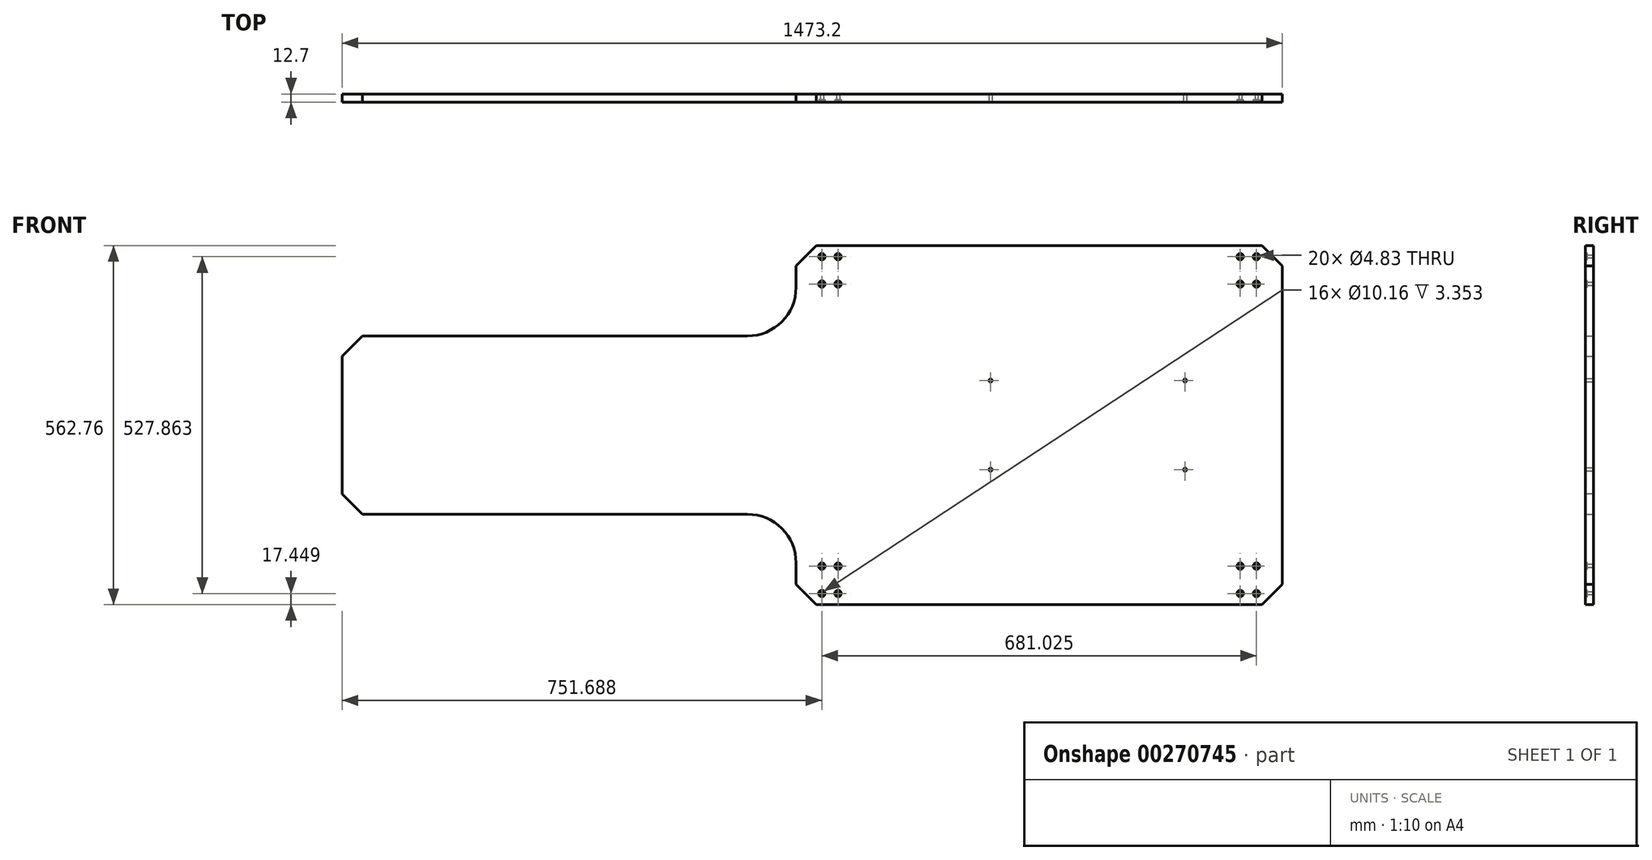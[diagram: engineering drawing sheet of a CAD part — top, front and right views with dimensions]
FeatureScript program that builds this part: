
annotation { "Feature Type Name" : "Feature", "Feature Type Description" : "" }
export const myFeature = defineFeature(function(context is Context, id is Id, definition is map)
    precondition{}
    {
        {
            var Q0;
            Q0=qCreatedBy(makeId("Front.planeOp"),FACE);
            var sketch = newSketch(context, id + "F0", { "sketchPlane" : qUnion([Q0])});
            skLineSegment(sketch, "E0.bottom", {"start": v(381, 281.38) * mm, "end": v(-381, 281.38) * mm});
            skLineSegment(sketch, "E0.top", {"start": v(381, -281.38) * mm, "end": v(-381, -281.38) * mm});
            skLineSegment(sketch, "E0.left", {"start": v(381, 281.38) * mm, "end": v(381, -281.38) * mm});
            skLineSegment(sketch, "E0.right", {"start": v(-381, 281.38) * mm, "end": v(-381, 139.7) * mm});
            skPoint(sketch, "E0.middle", {"position": v(0, 0) * mm});
            skPoint(sketch, "E1.left.start.orphan", {"position": v(330.2, 127) * mm});
            skPoint(sketch, "E2.orphan", {"position": v(330.2, -127) * mm});
            skLineSegment(sketch, "E3.trimOffspring", {"start": v(-381, -139.7) * mm, "end": v(-381, -281.38) * mm});
            skPoint(sketch, "E4.middle", {"position": v(-381, 0) * mm});
            skPoint(sketch, "E5.orphan", {"position": v(-381, -127) * mm});
            skLineSegment(sketch, "E6", {"start": v(-1092.2, 0) * mm, "end": v(-1092.2, 139.7) * mm});
            skLineSegment(sketch, "E7", {"start": v(-1092.2, 139.7) * mm, "end": v(-381, 139.7) * mm});
            skLineSegment(sketch, "E8", {"start": v(-400.15, -139.7) * mm, "end": v(-1092.2, -139.7) * mm});
            skLineSegment(sketch, "E9", {"start": v(-1092.2, -139.7) * mm, "end": v(-1092.2, 0) * mm});
            skLineSegment(sketch, "E10", {"start": v(-400.15, -139.7) * mm, "end": v(-381, -139.7) * mm});
            skLineSegment(sketch, "E11", {"start": v(381, 0) * mm, "end": v(381, 139.7) * mm});
            skLineSegment(sketch, "E12", {"start": v(381, 139.7) * mm, "end": v(381, -139.7) * mm});
            skLineSegment(sketch, "E13", {"start": v(381, -139.7) * mm, "end": v(381, 0) * mm});
            skLineSegment(sketch, "E14", {"start": v(381, -69.85) * mm, "end": v(228.6, -69.85) * mm});
            skLineSegment(sketch, "E15", {"start": v(381, 139.7) * mm, "end": v(381, 69.85) * mm});
            skLineSegment(sketch, "E16", {"start": v(381, 69.85) * mm, "end": v(228.6, 69.85) * mm});
            skLineSegment(sketch, "E17", {"start": v(228.6, 69.85) * mm, "end": v(-76.2, 69.85) * mm});
            skLineSegment(sketch, "E18", {"start": v(228.6, -69.85) * mm, "end": v(-76.2, -69.85) * mm});
            skPoint(sketch, "E19", {"position": v(-76.2, 69.85) * mm});
            skPoint(sketch, "E20", {"position": v(-76.2, -69.85) * mm});
            skPoint(sketch, "E21", {"position": v(228.6, -69.85) * mm});
            skPoint(sketch, "E22", {"position": v(228.6, 69.85) * mm});
            skSolve(sketch);
        }
        {
            var Q0;
            Q0 = qSketchRegion(id + "F0", true);
            extrude(context, id + "F1", {"entities" : qUnion([Q0]), "depth" : 12.7 * mm});
        }
        {
            var Q0;
            Q0=makeQuery(id+"F1.opExtrude","SWEPT_EDGE",EDGE,{"disambiguationData":[OSD([sQuery(id+"F0.wireOp",EDGE,"E0.top"),sQuery(id+"F0.wireOp",EDGE,"E3.trimOffspring")])]});
            var Q1;
            Q1=makeQuery(id+"F1.opExtrude","SWEPT_EDGE",EDGE,{"disambiguationData":[OSD([sQuery(id+"F0.wireOp",EDGE,"E0.top"),sQuery(id+"F0.wireOp",EDGE,"E0.left")])]});
            var Q2;
            Q2=makeQuery(id+"F1.opExtrude","SWEPT_EDGE",EDGE,{"disambiguationData":[OSD([sQuery(id+"F0.wireOp",EDGE,"E0.bottom"),sQuery(id+"F0.wireOp",EDGE,"E0.left")])]});
            var Q3;
            Q3=makeQuery(id+"F1.opExtrude","SWEPT_EDGE",EDGE,{"disambiguationData":[OSD([sQuery(id+"F0.wireOp",EDGE,"E0.bottom"),sQuery(id+"F0.wireOp",EDGE,"E0.right")])]});
            var Q4;
            Q4=makeQuery(id+"F1.opExtrude","SWEPT_EDGE",EDGE,{"disambiguationData":[OSD([sQuery(id+"F0.wireOp",EDGE,"E1.bottom"),sQuery(id+"F0.wireOp",EDGE,"E1.right")])]});
            var Q5;
            Q5=makeQuery(id+"F1.opExtrude","SWEPT_EDGE",EDGE,{"disambiguationData":[OSD([sQuery(id+"F0.wireOp",EDGE,"E1.top"),sQuery(id+"F0.wireOp",EDGE,"E1.right")])]});
            var Q6;
            Q6=makeQuery(id+"F1.opExtrude","SWEPT_EDGE",EDGE,{"disambiguationData":[OSD([sQuery(id+"F0.wireOp",EDGE,"E8"),sQuery(id+"F0.wireOp",EDGE,"E9")])]});
            var Q7;
            Q7=makeQuery(id+"F1.opExtrude","SWEPT_EDGE",EDGE,{"disambiguationData":[OSD([sQuery(id+"F0.wireOp",EDGE,"E6"),sQuery(id+"F0.wireOp",EDGE,"E7")])]});
            chamfer(context, id + "F2", {"entities" : qUnion([Q0, Q1, Q2, Q3, Q4, Q5, Q6, Q7]), "width" : 31.75 * mm, "tangentPropagation" : true});
        }
        {
            var Q0;
            Q0=makeQuery(id+"F1.opExtrude","SWEPT_EDGE",EDGE,{"disambiguationData":[OSD([sQuery(id+"F0.wireOp",EDGE,"E1.top"),sQuery(id+"F0.wireOp",EDGE,"E3.trimOffspring")])]});
            var Q1;
            Q1=makeQuery(id+"F1.opExtrude","SWEPT_EDGE",EDGE,{"disambiguationData":[OSD([sQuery(id+"F0.wireOp",EDGE,"E0.right"),sQuery(id+"F0.wireOp",EDGE,"E1.bottom")])]});
            fillet(context, id + "F3", {"entities" : qUnion([Q0, Q1]), "radius" : 76.2 * mm, "tangentPropagation" : true, "allowEdgeOverflow" : false});
        }
        {
            var Q0;
            Q0=makeQuery(id+"F1.opExtrude","CAP_FACE",FACE,{"disambiguationData":[OSD([sQuery(id+"F0.wireOp",EDGE,"E0.bottom"),sQuery(id+"F0.wireOp",EDGE,"E0.top"),sQuery(id+"F0.wireOp",EDGE,"E0.left"),sQuery(id+"F0.wireOp",EDGE,"E0.right"),sQuery(id+"F0.wireOp",EDGE,"E3.trimOffspring"),sQuery(id+"F0.wireOp",EDGE,"E6"),sQuery(id+"F0.wireOp",EDGE,"E7"),sQuery(id+"F0.wireOp",EDGE,"E8"),sQuery(id+"F0.wireOp",EDGE,"E9"),sQuery(id+"F0.wireOp",EDGE,"E10")])],"isStart":false});
            var sketch = newSketch(context, id + "F4", { "sketchPlane" : qUnion([Q0])});
            skPoint(sketch, "E23", {"position": v(340.51, -221.06) * mm});
            skPoint(sketch, "E24", {"position": v(315.11, -221.06) * mm});
            skPoint(sketch, "E25", {"position": v(315.11, -263.93) * mm});
            skPoint(sketch, "E26", {"position": v(340.51, -263.93) * mm});
            skPoint(sketch, "E27.MirrorP", {"position": v(315.11, 263.93) * mm});
            skPoint(sketch, "E28.MirrorP", {"position": v(315.11, 221.06) * mm});
            skPoint(sketch, "E29.MirrorP", {"position": v(340.51, 221.06) * mm});
            skPoint(sketch, "E30.MirrorP", {"position": v(340.51, 263.93) * mm});
            skPoint(sketch, "E31.MirrorP", {"position": v(-315.11, -221.06) * mm});
            skPoint(sketch, "E32.MirrorP", {"position": v(-340.51, -221.06) * mm});
            skPoint(sketch, "E33.MirrorP", {"position": v(-340.51, -263.93) * mm});
            skPoint(sketch, "E34.MirrorP", {"position": v(-315.11, -263.93) * mm});
            skPoint(sketch, "E35.MirrorP", {"position": v(-315.11, 263.93) * mm});
            skPoint(sketch, "E36.MirrorP", {"position": v(-340.51, 263.93) * mm});
            skPoint(sketch, "E37.MirrorP", {"position": v(-340.51, 221.06) * mm});
            skPoint(sketch, "E38.MirrorP", {"position": v(-315.11, 221.06) * mm});
            skSolve(sketch);
        }
        {
            var Q0;
            Q0=sQuery(id+"F4.wireOp",VERTEX,"E36.MirrorP");
            var Q1;
            Q1=sQuery(id+"F4.wireOp",VERTEX,"E35.MirrorP");
            var Q2;
            Q2=sQuery(id+"F4.wireOp",VERTEX,"E38.MirrorP");
            var Q3;
            Q3=sQuery(id+"F4.wireOp",VERTEX,"E37.MirrorP");
            var Q4;
            Q4=sQuery(id+"F4.wireOp",VERTEX,"E27.MirrorP");
            var Q5;
            Q5=sQuery(id+"F4.wireOp",VERTEX,"E30.MirrorP");
            var Q6;
            Q6=sQuery(id+"F4.wireOp",VERTEX,"E29.MirrorP");
            var Q7;
            Q7=sQuery(id+"F4.wireOp",VERTEX,"E28.MirrorP");
            var Q8;
            Q8=sQuery(id+"F4.wireOp",VERTEX,"E23");
            var Q9;
            Q9=sQuery(id+"F4.wireOp",VERTEX,"E24");
            var Q10;
            Q10=sQuery(id+"F4.wireOp",VERTEX,"E25");
            var Q11;
            Q11=sQuery(id+"F4.wireOp",VERTEX,"E26");
            var Q12;
            Q12=sQuery(id+"F4.wireOp",VERTEX,"E31.MirrorP");
            var Q13;
            Q13=sQuery(id+"F4.wireOp",VERTEX,"E32.MirrorP");
            var Q14;
            Q14=sQuery(id+"F4.wireOp",VERTEX,"E33.MirrorP");
            var Q15;
            Q15=sQuery(id+"F4.wireOp",VERTEX,"E34.MirrorP");
            var Q16;
            Q16=makeQuery(id+"F1.opExtrude","SWEPT_BODY",BODY,{"disambiguationData":[OSD([sQuery(id+"F0.wireOp",EDGE,"E0.bottom"),sQuery(id+"F0.wireOp",EDGE,"E0.top"),sQuery(id+"F0.wireOp",EDGE,"E0.left"),sQuery(id+"F0.wireOp",EDGE,"E0.right"),sQuery(id+"F0.wireOp",EDGE,"E3.trimOffspring"),sQuery(id+"F0.wireOp",EDGE,"E6"),sQuery(id+"F0.wireOp",EDGE,"E7"),sQuery(id+"F0.wireOp",EDGE,"E8"),sQuery(id+"F0.wireOp",EDGE,"E9"),sQuery(id+"F0.wireOp",EDGE,"E10")])]});
            hole(context, id + "F5", {"style" : HoleStyle.C_BORE, "endStyle" : HoleEndStyle.THROUGH, "holeDiameter" : 4.83 * mm, "cBoreDiameter" : 10.16 * mm, "cBoreDepth" : 3.35 * mm, "tappedDepth" : 12.7 * mm, "tapClearance" : 3, "locations" : qUnion([Q0, Q1, Q2, Q3, Q4, Q5, Q6, Q7, Q8, Q9, Q10, Q11, Q12, Q13, Q14, Q15]), "scope" : qUnion([Q16])});
        }
        {
            var Q0;
            Q0=makeQuery(id+"F1.opExtrude","CAP_FACE",FACE,{"disambiguationData":[OSD([sQuery(id+"F0.wireOp",EDGE,"E0.bottom"),sQuery(id+"F0.wireOp",EDGE,"E0.top"),sQuery(id+"F0.wireOp",EDGE,"E0.left"),sQuery(id+"F0.wireOp",EDGE,"E0.right"),sQuery(id+"F0.wireOp",EDGE,"E3.trimOffspring"),sQuery(id+"F0.wireOp",EDGE,"E6"),sQuery(id+"F0.wireOp",EDGE,"E7"),sQuery(id+"F0.wireOp",EDGE,"E8"),sQuery(id+"F0.wireOp",EDGE,"E9"),sQuery(id+"F0.wireOp",EDGE,"E10"),sQuery(id+"F0.wireOp",EDGE,"E12"),sQuery(id+"F0.wireOp",EDGE,"E13"),sQuery(id+"F0.wireOp",EDGE,"E15")])],"isStart":false});
            var sketch = newSketch(context, id + "F6", { "sketchPlane" : qUnion([Q0])});
            skLineSegment(sketch, "E39", {"start": v(381, 0) * mm, "end": v(381, 139.7) * mm});
            skLineSegment(sketch, "E40", {"start": v(381, 139.7) * mm, "end": v(381, -139.7) * mm});
            skLineSegment(sketch, "E41", {"start": v(381, -139.7) * mm, "end": v(381, 0) * mm});
            skLineSegment(sketch, "E42", {"start": v(381, -69.85) * mm, "end": v(228.6, -69.85) * mm});
            skLineSegment(sketch, "E43", {"start": v(228.6, -69.85) * mm, "end": v(-76.2, -69.85) * mm});
            skLineSegment(sketch, "E44", {"start": v(381, 69.85) * mm, "end": v(228.6, 69.85) * mm});
            skPoint(sketch, "E44.endSnap0", {"position": v(381, 69.85) * mm});
            skLineSegment(sketch, "E45", {"start": v(228.6, 69.85) * mm, "end": v(-76.2, 69.85) * mm});
            skPoint(sketch, "E46", {"position": v(-76.2, 69.85) * mm});
            skPoint(sketch, "E47", {"position": v(228.6, 69.85) * mm});
            skPoint(sketch, "E48", {"position": v(228.6, -69.85) * mm});
            skPoint(sketch, "E49", {"position": v(-76.2, -69.85) * mm});
            skSolve(sketch);
        }
        {
            var Q0;
            Q0=sQuery(id+"F6.wireOp",VERTEX,"E46");
            var Q1;
            Q1=sQuery(id+"F6.wireOp",VERTEX,"E47");
            var Q2;
            Q2=sQuery(id+"F6.wireOp",VERTEX,"E48");
            var Q3;
            Q3=sQuery(id+"F6.wireOp",VERTEX,"E49");
            var Q4;
            Q4=makeQuery(id+"F1.opExtrude","SWEPT_BODY",BODY,{"disambiguationData":[OSD([sQuery(id+"F0.wireOp",EDGE,"E0.bottom"),sQuery(id+"F0.wireOp",EDGE,"E0.top"),sQuery(id+"F0.wireOp",EDGE,"E0.left"),sQuery(id+"F0.wireOp",EDGE,"E0.right"),sQuery(id+"F0.wireOp",EDGE,"E3.trimOffspring"),sQuery(id+"F0.wireOp",EDGE,"E6"),sQuery(id+"F0.wireOp",EDGE,"E7"),sQuery(id+"F0.wireOp",EDGE,"E8"),sQuery(id+"F0.wireOp",EDGE,"E9"),sQuery(id+"F0.wireOp",EDGE,"E10"),sQuery(id+"F0.wireOp",EDGE,"E12"),sQuery(id+"F0.wireOp",EDGE,"E13"),sQuery(id+"F0.wireOp",EDGE,"E15")])]});
            hole(context, id + "F7", {"style" : HoleStyle.SIMPLE, "endStyle" : HoleEndStyle.THROUGH, "holeDiameter" : 4.83 * mm, "tappedDepth" : 12.7 * mm, "tapClearance" : 3, "locations" : qUnion([Q0, Q1, Q2, Q3]), "scope" : qUnion([Q4])});
        }
    });
